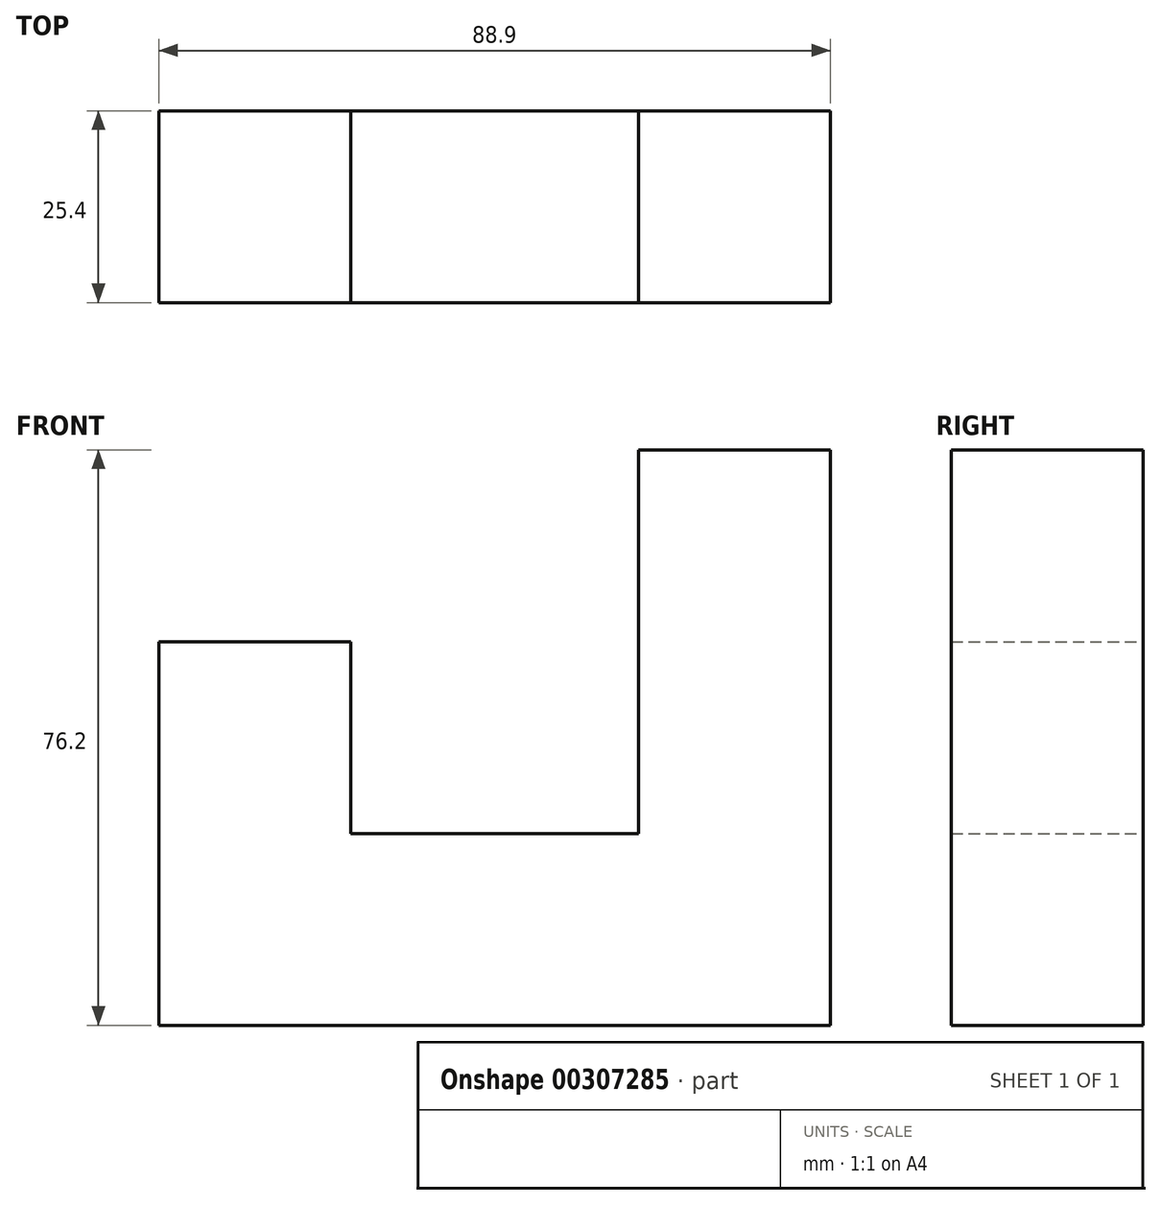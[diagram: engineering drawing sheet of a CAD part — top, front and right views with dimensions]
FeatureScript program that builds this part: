
annotation { "Feature Type Name" : "Feature", "Feature Type Description" : "" }
export const myFeature = defineFeature(function(context is Context, id is Id, definition is map)
    precondition{}
    {
        {
            var Q0;
            Q0=qCreatedBy(makeId("Front.planeOp"),FACE);
            var sketch = newSketch(context, id + "F0", { "sketchPlane" : qUnion([Q0])});
            skLineSegment(sketch, "E0", {"start": v(-45.76, -25.4) * mm, "end": v(43.14, -25.4) * mm});
            skLineSegment(sketch, "E1", {"start": v(43.14, -25.4) * mm, "end": v(43.14, 50.8) * mm});
            skLineSegment(sketch, "E2", {"start": v(43.14, 50.8) * mm, "end": v(17.74, 50.8) * mm});
            skLineSegment(sketch, "E3", {"start": v(17.74, 50.8) * mm, "end": v(17.74, 0) * mm});
            skLineSegment(sketch, "E4", {"start": v(17.74, 0) * mm, "end": v(-20.36, 0) * mm});
            skLineSegment(sketch, "E5", {"start": v(-20.36, 0) * mm, "end": v(-20.36, 25.4) * mm});
            skLineSegment(sketch, "E6", {"start": v(-20.36, 25.4) * mm, "end": v(-45.76, 25.4) * mm});
            skLineSegment(sketch, "E7", {"start": v(-45.76, 25.4) * mm, "end": v(-45.76, -25.4) * mm});
            skSolve(sketch);
        }
        {
            var Q0;
            Q0=makeQuery(id+"F0.imprint","IMPRINT",FACE,{"disambiguationData":[TD([[makeQuery(id+"F0.imprint","IMPRINT",EDGE,{"derivedFrom":sQuery(id+"F0.wireOp",EDGE,"E0")}),1.0]])]});
            extrude(context, id + "F1", {"entities" : qUnion([Q0]), "depth" : 25.4 * mm});
        }
    });
